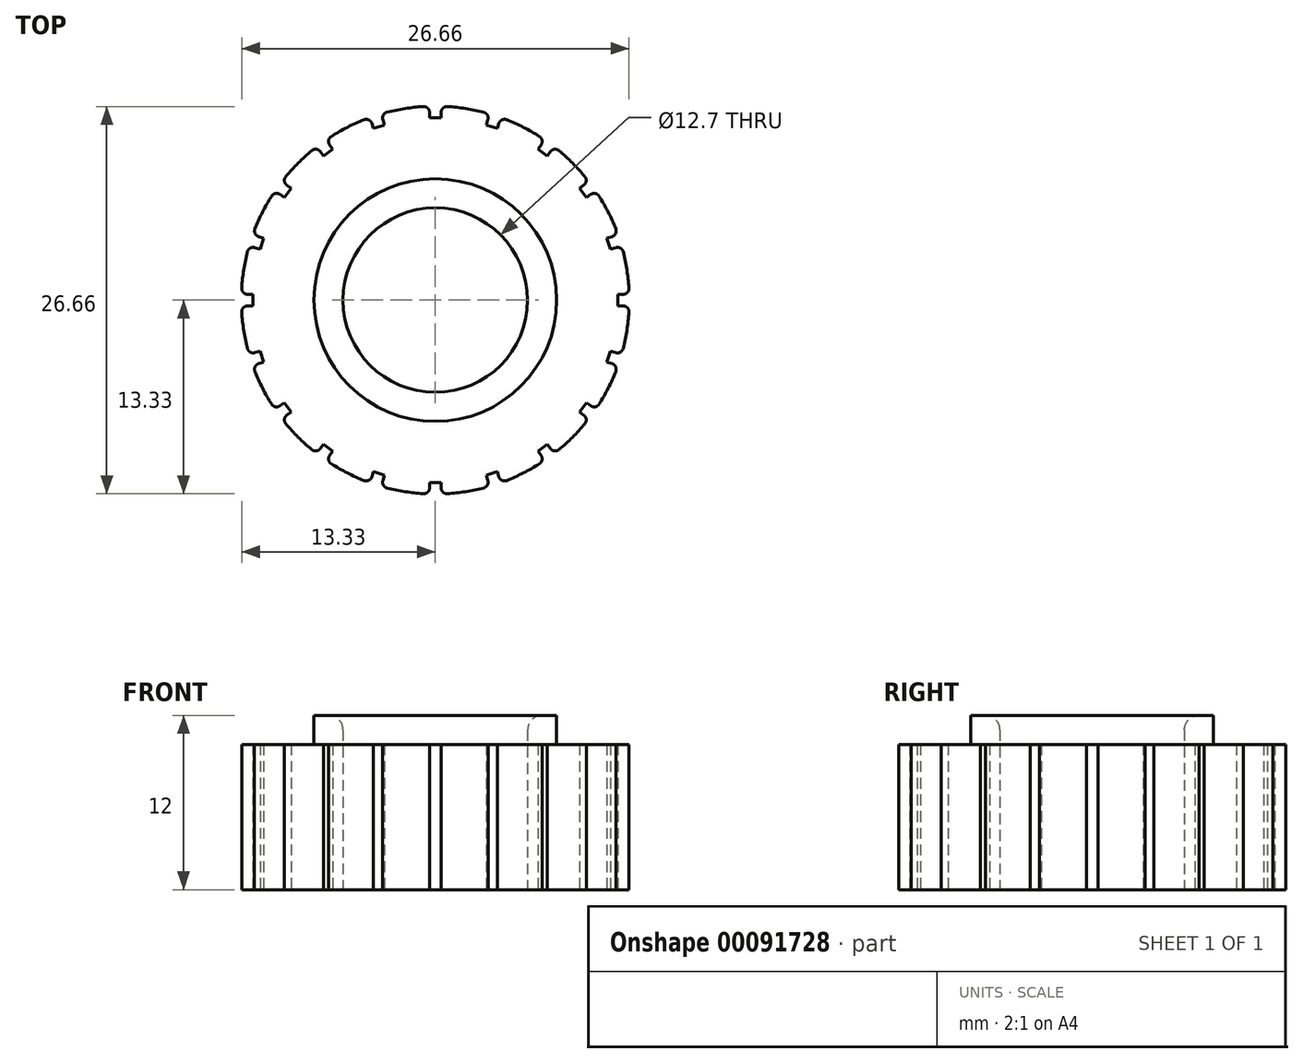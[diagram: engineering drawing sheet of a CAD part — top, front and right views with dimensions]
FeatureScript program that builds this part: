
annotation { "Feature Type Name" : "Feature", "Feature Type Description" : "" }
export const myFeature = defineFeature(function(context is Context, id is Id, definition is map)
    precondition{}
    {
        {
            var Q0;
            Q0=qCreatedBy(makeId("Top.planeOp"),FACE);
            var sketch = newSketch(context, id + "F0", { "sketchPlane" : qUnion([Q0])});
            skCircle(sketch, "E0", {"center": v(0, 0) * mm, "radius": 6.35 * mm});
            skCircle(sketch, "E1", {"center": v(0, 0) * mm, "radius": 8.35 * mm});
            skCircle(sketch, "E2", {"center": v(0, 0) * mm, "radius": 13.35 * mm});
            skLineSegment(sketch, "E3", {"start": v(0, 0) * mm, "end": v(0, 13.35) * mm, "construction": true});
            skLineSegment(sketch, "E4", {"start": v(-0.4, 12.93) * mm, "end": v(-0.4, 12.55) * mm});
            skLineSegment(sketch, "E5", {"start": v(-0.4, 12.55) * mm, "end": v(0.4, 12.55) * mm});
            skLineSegment(sketch, "E6", {"start": v(0.4, 12.55) * mm, "end": v(0.4, 12.93) * mm});
            skArc(sketch, "E7", {"start": v(-0.4, 12.93) * mm, "mid": v(-0.53, 13.22) * mm, "end": v(-0.82, 13.32) * mm});
            skPoint(sketch, "E7.second.point", {"position": v(-0.82, 13.32) * mm});
            skPoint(sketch, "E7.third.point.positionSnap0", {"position": v(-0.4, 12.93) * mm});
            skArc(sketch, "E8.MirrorCS", {"start": v(0.4, 12.93) * mm, "mid": v(0.53, 13.22) * mm, "end": v(0.82, 13.32) * mm});
            skArc(sketch, "E9.1.0", {"start": v(-4.37, 12.17) * mm, "mid": v(-4.58, 12.4) * mm, "end": v(-4.9, 12.42) * mm});
            skLineSegment(sketch, "E9.1.1", {"start": v(-4.37, 12.17) * mm, "end": v(-4.26, 11.81) * mm});
            skLineSegment(sketch, "E9.1.2", {"start": v(-4.26, 11.81) * mm, "end": v(-3.5, 12.06) * mm});
            skLineSegment(sketch, "E9.1.3", {"start": v(-3.5, 12.06) * mm, "end": v(-3.61, 12.42) * mm});
            skArc(sketch, "E9.1.4", {"start": v(-3.61, 12.42) * mm, "mid": v(-3.58, 12.73) * mm, "end": v(-3.33, 12.93) * mm});
            skArc(sketch, "E9.2.0", {"start": v(-7.92, 10.22) * mm, "mid": v(-8.2, 10.38) * mm, "end": v(-8.5, 10.3) * mm});
            skLineSegment(sketch, "E9.2.1", {"start": v(-7.92, 10.22) * mm, "end": v(-7.7, 9.92) * mm});
            skLineSegment(sketch, "E9.2.2", {"start": v(-7.7, 9.92) * mm, "end": v(-7.05, 10.39) * mm});
            skLineSegment(sketch, "E9.2.3", {"start": v(-7.05, 10.39) * mm, "end": v(-7.27, 10.7) * mm});
            skArc(sketch, "E9.2.4", {"start": v(-7.27, 10.7) * mm, "mid": v(-7.34, 11) * mm, "end": v(-7.16, 11.26) * mm});
            skArc(sketch, "E9.3.0", {"start": v(-10.7, 7.27) * mm, "mid": v(-11, 7.34) * mm, "end": v(-11.26, 7.16) * mm});
            skLineSegment(sketch, "E9.3.1", {"start": v(-10.7, 7.27) * mm, "end": v(-10.39, 7.05) * mm});
            skLineSegment(sketch, "E9.3.2", {"start": v(-10.39, 7.05) * mm, "end": v(-9.92, 7.7) * mm});
            skLineSegment(sketch, "E9.3.3", {"start": v(-9.92, 7.7) * mm, "end": v(-10.22, 7.92) * mm});
            skArc(sketch, "E9.3.4", {"start": v(-10.22, 7.92) * mm, "mid": v(-10.38, 8.2) * mm, "end": v(-10.3, 8.5) * mm});
            skArc(sketch, "E9.4.0", {"start": v(-12.42, 3.61) * mm, "mid": v(-12.73, 3.58) * mm, "end": v(-12.93, 3.33) * mm});
            skLineSegment(sketch, "E9.4.1", {"start": v(-12.42, 3.61) * mm, "end": v(-12.06, 3.5) * mm});
            skLineSegment(sketch, "E9.4.2", {"start": v(-12.06, 3.5) * mm, "end": v(-11.81, 4.26) * mm});
            skLineSegment(sketch, "E9.4.3", {"start": v(-11.81, 4.26) * mm, "end": v(-12.17, 4.37) * mm});
            skArc(sketch, "E9.4.4", {"start": v(-12.17, 4.37) * mm, "mid": v(-12.4, 4.58) * mm, "end": v(-12.42, 4.9) * mm});
            skArc(sketch, "E9.5.0", {"start": v(-12.93, -0.4) * mm, "mid": v(-13.22, -0.53) * mm, "end": v(-13.32, -0.82) * mm});
            skLineSegment(sketch, "E9.5.1", {"start": v(-12.93, -0.4) * mm, "end": v(-12.55, -0.4) * mm});
            skLineSegment(sketch, "E9.5.2", {"start": v(-12.55, -0.4) * mm, "end": v(-12.55, 0.4) * mm});
            skLineSegment(sketch, "E9.5.3", {"start": v(-12.55, 0.4) * mm, "end": v(-12.93, 0.4) * mm});
            skArc(sketch, "E9.5.4", {"start": v(-12.93, 0.4) * mm, "mid": v(-13.22, 0.53) * mm, "end": v(-13.32, 0.82) * mm});
            skArc(sketch, "E9.6.0", {"start": v(-12.17, -4.37) * mm, "mid": v(-12.4, -4.58) * mm, "end": v(-12.42, -4.9) * mm});
            skLineSegment(sketch, "E9.6.1", {"start": v(-12.17, -4.37) * mm, "end": v(-11.81, -4.26) * mm});
            skLineSegment(sketch, "E9.6.2", {"start": v(-11.81, -4.26) * mm, "end": v(-12.06, -3.5) * mm});
            skLineSegment(sketch, "E9.6.3", {"start": v(-12.06, -3.5) * mm, "end": v(-12.42, -3.61) * mm});
            skArc(sketch, "E9.6.4", {"start": v(-12.42, -3.61) * mm, "mid": v(-12.73, -3.58) * mm, "end": v(-12.93, -3.33) * mm});
            skArc(sketch, "E9.7.0", {"start": v(-10.22, -7.92) * mm, "mid": v(-10.38, -8.2) * mm, "end": v(-10.3, -8.5) * mm});
            skLineSegment(sketch, "E9.7.1", {"start": v(-10.22, -7.92) * mm, "end": v(-9.92, -7.7) * mm});
            skLineSegment(sketch, "E9.7.2", {"start": v(-9.92, -7.7) * mm, "end": v(-10.39, -7.05) * mm});
            skLineSegment(sketch, "E9.7.3", {"start": v(-10.39, -7.05) * mm, "end": v(-10.7, -7.27) * mm});
            skArc(sketch, "E9.7.4", {"start": v(-10.7, -7.27) * mm, "mid": v(-11, -7.34) * mm, "end": v(-11.26, -7.16) * mm});
            skArc(sketch, "E9.8.0", {"start": v(-7.27, -10.7) * mm, "mid": v(-7.34, -11) * mm, "end": v(-7.16, -11.26) * mm});
            skLineSegment(sketch, "E9.8.1", {"start": v(-7.27, -10.7) * mm, "end": v(-7.05, -10.39) * mm});
            skLineSegment(sketch, "E9.8.2", {"start": v(-7.05, -10.39) * mm, "end": v(-7.7, -9.92) * mm});
            skLineSegment(sketch, "E9.8.3", {"start": v(-7.7, -9.92) * mm, "end": v(-7.92, -10.22) * mm});
            skArc(sketch, "E9.8.4", {"start": v(-7.92, -10.22) * mm, "mid": v(-8.2, -10.38) * mm, "end": v(-8.5, -10.3) * mm});
            skArc(sketch, "E9.9.0", {"start": v(-3.61, -12.42) * mm, "mid": v(-3.58, -12.73) * mm, "end": v(-3.33, -12.93) * mm});
            skLineSegment(sketch, "E9.9.1", {"start": v(-3.61, -12.42) * mm, "end": v(-3.5, -12.06) * mm});
            skLineSegment(sketch, "E9.9.2", {"start": v(-3.5, -12.06) * mm, "end": v(-4.26, -11.81) * mm});
            skLineSegment(sketch, "E9.9.3", {"start": v(-4.26, -11.81) * mm, "end": v(-4.37, -12.17) * mm});
            skArc(sketch, "E9.9.4", {"start": v(-4.37, -12.17) * mm, "mid": v(-4.58, -12.4) * mm, "end": v(-4.9, -12.42) * mm});
            skArc(sketch, "E9.10.0", {"start": v(0.4, -12.93) * mm, "mid": v(0.53, -13.22) * mm, "end": v(0.82, -13.32) * mm});
            skLineSegment(sketch, "E9.10.1", {"start": v(0.4, -12.93) * mm, "end": v(0.4, -12.55) * mm});
            skLineSegment(sketch, "E9.10.2", {"start": v(0.4, -12.55) * mm, "end": v(-0.4, -12.55) * mm});
            skLineSegment(sketch, "E9.10.3", {"start": v(-0.4, -12.55) * mm, "end": v(-0.4, -12.93) * mm});
            skArc(sketch, "E9.10.4", {"start": v(-0.4, -12.93) * mm, "mid": v(-0.53, -13.22) * mm, "end": v(-0.82, -13.32) * mm});
            skArc(sketch, "E9.11.0", {"start": v(4.37, -12.17) * mm, "mid": v(4.58, -12.4) * mm, "end": v(4.9, -12.42) * mm});
            skLineSegment(sketch, "E9.11.1", {"start": v(4.37, -12.17) * mm, "end": v(4.26, -11.81) * mm});
            skLineSegment(sketch, "E9.11.2", {"start": v(4.26, -11.81) * mm, "end": v(3.5, -12.06) * mm});
            skLineSegment(sketch, "E9.11.3", {"start": v(3.5, -12.06) * mm, "end": v(3.61, -12.42) * mm});
            skArc(sketch, "E9.11.4", {"start": v(3.61, -12.42) * mm, "mid": v(3.58, -12.73) * mm, "end": v(3.33, -12.93) * mm});
            skArc(sketch, "E9.12.0", {"start": v(7.92, -10.22) * mm, "mid": v(8.2, -10.38) * mm, "end": v(8.5, -10.3) * mm});
            skLineSegment(sketch, "E9.12.1", {"start": v(7.92, -10.22) * mm, "end": v(7.7, -9.92) * mm});
            skLineSegment(sketch, "E9.12.2", {"start": v(7.7, -9.92) * mm, "end": v(7.05, -10.39) * mm});
            skLineSegment(sketch, "E9.12.3", {"start": v(7.05, -10.39) * mm, "end": v(7.27, -10.7) * mm});
            skArc(sketch, "E9.12.4", {"start": v(7.27, -10.7) * mm, "mid": v(7.34, -11) * mm, "end": v(7.16, -11.26) * mm});
            skArc(sketch, "E9.13.0", {"start": v(10.7, -7.27) * mm, "mid": v(11, -7.34) * mm, "end": v(11.26, -7.16) * mm});
            skLineSegment(sketch, "E9.13.1", {"start": v(10.7, -7.27) * mm, "end": v(10.39, -7.05) * mm});
            skLineSegment(sketch, "E9.13.2", {"start": v(10.39, -7.05) * mm, "end": v(9.92, -7.7) * mm});
            skLineSegment(sketch, "E9.13.3", {"start": v(9.92, -7.7) * mm, "end": v(10.22, -7.92) * mm});
            skArc(sketch, "E9.13.4", {"start": v(10.22, -7.92) * mm, "mid": v(10.38, -8.2) * mm, "end": v(10.3, -8.5) * mm});
            skArc(sketch, "E9.14.0", {"start": v(12.42, -3.61) * mm, "mid": v(12.73, -3.58) * mm, "end": v(12.93, -3.33) * mm});
            skLineSegment(sketch, "E9.14.1", {"start": v(12.42, -3.61) * mm, "end": v(12.06, -3.5) * mm});
            skLineSegment(sketch, "E9.14.2", {"start": v(12.06, -3.5) * mm, "end": v(11.81, -4.26) * mm});
            skLineSegment(sketch, "E9.14.3", {"start": v(11.81, -4.26) * mm, "end": v(12.17, -4.37) * mm});
            skArc(sketch, "E9.14.4", {"start": v(12.17, -4.37) * mm, "mid": v(12.4, -4.58) * mm, "end": v(12.42, -4.9) * mm});
            skArc(sketch, "E9.15.0", {"start": v(12.93, 0.4) * mm, "mid": v(13.22, 0.53) * mm, "end": v(13.32, 0.82) * mm});
            skLineSegment(sketch, "E9.15.1", {"start": v(12.93, 0.4) * mm, "end": v(12.55, 0.4) * mm});
            skLineSegment(sketch, "E9.15.2", {"start": v(12.55, 0.4) * mm, "end": v(12.55, -0.4) * mm});
            skLineSegment(sketch, "E9.15.3", {"start": v(12.55, -0.4) * mm, "end": v(12.93, -0.4) * mm});
            skArc(sketch, "E9.15.4", {"start": v(12.93, -0.4) * mm, "mid": v(13.22, -0.53) * mm, "end": v(13.32, -0.82) * mm});
            skArc(sketch, "E9.16.0", {"start": v(12.17, 4.37) * mm, "mid": v(12.4, 4.58) * mm, "end": v(12.42, 4.9) * mm});
            skLineSegment(sketch, "E9.16.1", {"start": v(12.17, 4.37) * mm, "end": v(11.81, 4.26) * mm});
            skLineSegment(sketch, "E9.16.2", {"start": v(11.81, 4.26) * mm, "end": v(12.06, 3.5) * mm});
            skLineSegment(sketch, "E9.16.3", {"start": v(12.06, 3.5) * mm, "end": v(12.42, 3.61) * mm});
            skArc(sketch, "E9.16.4", {"start": v(12.42, 3.61) * mm, "mid": v(12.73, 3.58) * mm, "end": v(12.93, 3.33) * mm});
            skArc(sketch, "E9.17.0", {"start": v(10.22, 7.92) * mm, "mid": v(10.38, 8.2) * mm, "end": v(10.3, 8.5) * mm});
            skLineSegment(sketch, "E9.17.1", {"start": v(10.22, 7.92) * mm, "end": v(9.92, 7.7) * mm});
            skLineSegment(sketch, "E9.17.2", {"start": v(9.92, 7.7) * mm, "end": v(10.39, 7.05) * mm});
            skLineSegment(sketch, "E9.17.3", {"start": v(10.39, 7.05) * mm, "end": v(10.7, 7.27) * mm});
            skArc(sketch, "E9.17.4", {"start": v(10.7, 7.27) * mm, "mid": v(11, 7.34) * mm, "end": v(11.26, 7.16) * mm});
            skArc(sketch, "E9.18.0", {"start": v(7.27, 10.7) * mm, "mid": v(7.34, 11) * mm, "end": v(7.16, 11.26) * mm});
            skLineSegment(sketch, "E9.18.1", {"start": v(7.27, 10.7) * mm, "end": v(7.05, 10.39) * mm});
            skLineSegment(sketch, "E9.18.2", {"start": v(7.05, 10.39) * mm, "end": v(7.7, 9.92) * mm});
            skLineSegment(sketch, "E9.18.3", {"start": v(7.7, 9.92) * mm, "end": v(7.92, 10.22) * mm});
            skArc(sketch, "E9.18.4", {"start": v(7.92, 10.22) * mm, "mid": v(8.2, 10.38) * mm, "end": v(8.5, 10.3) * mm});
            skArc(sketch, "E9.19.0", {"start": v(3.61, 12.42) * mm, "mid": v(3.58, 12.73) * mm, "end": v(3.33, 12.93) * mm});
            skLineSegment(sketch, "E9.19.1", {"start": v(3.61, 12.42) * mm, "end": v(3.5, 12.06) * mm});
            skLineSegment(sketch, "E9.19.2", {"start": v(3.5, 12.06) * mm, "end": v(4.26, 11.81) * mm});
            skLineSegment(sketch, "E9.19.3", {"start": v(4.26, 11.81) * mm, "end": v(4.37, 12.17) * mm});
            skArc(sketch, "E9.19.4", {"start": v(4.37, 12.17) * mm, "mid": v(4.58, 12.4) * mm, "end": v(4.9, 12.42) * mm});
            skSolve(sketch);
        }
        {
            var Q0;
            Q0=makeQuery(id+"F0.imprint","IMPRINT",FACE,{"disambiguationData":[TD([[makeQuery(id+"F0.imprint","IMPRINT",EDGE,{"derivedFrom":sQuery(id+"F0.wireOp",EDGE,"E0")}),-1.0]])]});
            extrude(context, id + "F1", {"entities" : qUnion([Q0]), "depth" : 12 * mm});
        }
        {
            var Q0;
            Q0=makeQuery(id+"F0.imprint","IMPRINT",FACE,{"disambiguationData":[TD([[makeQuery(id+"F0.imprint","IMPRINT",EDGE,{"derivedFrom":sQuery(id+"F0.wireOp",EDGE,"E1")}),-1.0]])]});
            extrude(context, id + "F2", {"entities" : qUnion([Q0]), "operationType" : NewBodyOperationType.ADD, "depth" : 10 * mm});
        }
        {
            var Q0;
            Q0=makeQuery(id+"F1.opExtrude","CAP_EDGE",EDGE,{"disambiguationData":[OSD([sQuery(id+"F0.wireOp",EDGE,"E0")])],"isStart":false});
            fillet(context, id + "F3", {"entities" : qUnion([Q0]), "radius" : 1 * mm, "tangentPropagation" : true, "allowEdgeOverflow" : false});
        }
    });
